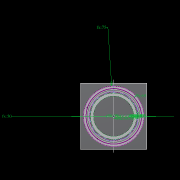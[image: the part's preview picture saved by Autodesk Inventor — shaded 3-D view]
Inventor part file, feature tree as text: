
AUTODESK INVENTOR PART (.ipt)
format: ipt  version: 2022.2 (Build 262287010, 287A)  size: 587,776 bytes
history: native  units: mm
features: other x19, extrude x19, sketch x12, pattern_circular x9, plane x3, fillet x2, move_body x2, revolve x2, draft x2, chamfer x2
ambient origin geometry x8: Origin, YZ Plane, XZ Plane, XY Plane, X Axis, Y Axis, Z Axis, Center Point
bodies: Solid5 (feature_tree)
feature tree (72):
  other  "CrossSection1"
  sketch  "Sketch7"  dims[d90=61.984365mm]
  other  "Roller1"
  other  "Roller2"
  sketch  "Sketch22"  dims[d167=8.972256mm]
  sketch  "Sketch2"  dims[d57=4.025mm]
  sketch  "Sketch23"  dims[d173=10.814812mm]
  other  "RevRoller1"
  fillet  "Fillet1"  Radius=59.246882mm
  pattern_circular  "Circular Pattern13"  Count=360  [1 undecoded]
  move_body  "Move Body7"
  revolve  "Revolution13"  [1 undecoded]
  fillet  "Fillet3"  Radius=0.025mm
  pattern_circular  "Circular Pattern14"  [2 undecoded]
  move_body  "Move Body6"
  revolve  "Revolution14"  [1 undecoded]
  other  "OuterRim_Top2"
  other  "OuterRim_Bottom2"
  plane  "Work Plane7"
  sketch  "Sketch47"  dims[d349=47.575591mm]
  sketch  "Sketch48"  dims[d350=47.575427mm]
  extrude  "Extrusion39"  Depth=50.0mm
  extrude  "Extrusion40"  Depth=50.0mm
  pattern_circular  "Circular Pattern28"  Angle=360.0deg  [1 undecoded]
  sketch  "Sketch49"  dims[d351=0.025mm d352=0.025mm d354=0.1mm d355=16.1595mm d356=16.159664mm d358=360.0deg d359=0.5mm d360=240.0mm d361=360.0deg d363=1.308997mm d367=8.1mm d370=0.1mm d371=1.0mm d372=1.308997mm d373=90.0deg d374=0.5mm d375=240.0mm d376=360.0deg d378=90.0deg d379=0.1mm d380=0.1mm d381=0.1mm d382=0.1mm d383=0.1mm d384=11.193516mm d385=0.0mm d386=0.0mm d391=50.0mm d392=75.0mm d393=1.5mm d394=1.5mm d395=1.5mm d396=1.5mm d397=90.0deg d398=90.0deg d399=90.0deg d400=75.0mm d401=11.193516mm d402=0.0mm d486=0.436332mm d487=0.5mm d488=2.0mm d489=0.0mm d490=20.0mm d495=2.5mm d496=8.0mm d506=13.856406mm d507=55.5mm d508=8.0mm d509=0.05mm d510=2.5mm d511=30.0deg d512=12.0mm d513=6.0mm d514=0.2mm d515=30.0deg d516=131.0mm d517=65.5mm d518=0.2mm d519=100.0mm d520=120.0mm d521=2.0mm d522=150.0mm d530=50.0mm d531=5.5mm d532=5.5mm d533=5.5mm d534=85.75mm d535=73.5mm d536=61.25mm d537=24.5mm d538=3.0mm d539=2.4mm d540=0.0mm d541=0.0mm d542=0.0mm d543=5.5mm d544=3.0mm d545=0.0mm d546=90.0mm d547=360.0deg d549=3.0mm d550=3.0mm d551=2.4mm d552=0.0mm d553=5.596758mm d554=0.0mm d555=2.4mm d556=0.0mm d557=5.596758mm d558=0.0mm d559=5.596758mm d560=0.0mm d561=90.0mm d562=360.0deg d564=60.0mm d565=360.0deg d567=5.5mm d568=5.5mm d569=3.0mm d570=0.0mm d571=5.596758mm d572=0.0mm d573=3.0mm d574=0.0mm d575=5.596758mm d576=0.0mm d577=90.0mm d578=360.0deg d580=60.0mm d581=360.0deg d584=20.0mm d585=8.0mm d587=1.75mm d589=3.0mm d592=2.0mm d593=12.0mm d594=12.0mm d600=0.5mm d601=2.0mm d602=45.0deg d603=0.5mm d604=2.0mm d605=45.0deg d606=0.436332mm d607=0.5mm d608=0.0mm d609=20.0mm d611=360.0deg d613=0.0mm d614=0.0mm d617=0.99971mm d618=100.0mm d620=69.0mm d621=3.0mm d622=5.5mm d623=5.596758mm d624=0.0mm d625=3.0mm d626=0.0mm d627=60.0mm d628=360.0deg d630=5.5mm d631=3.0mm d632=5.596758mm d633=0.0mm d634=2.593516mm d635=0.0mm d636=50.0mm d637=360.0deg d16=0.872665mm d17=0.872665mm d49=0.872665mm d50=0.872665mm d51=0.872665mm d52=0.872665mm d236=0.5mm d237=0.872665mm d238=0.5mm d239=0.872665mm d282=1.0mm d283=1.0mm d284=1.0mm d285=0.15mm d286=0.25mm d287=0.375mm d288=14.3117mm d289=0.75mm d290=20.594885mm d291=0.0625mm d292=0.75mm d293=0.375mm d405=0.5mm d406=0.872665mm d407=0.5mm d408=0.872665mm d413=0.5mm d414=0.872665mm d415=0.5mm d416=0.872665mm d417=0.5mm d418=0.872665mm d419=0.5mm d420=0.872665mm d421=0.872665mm d431=0.5mm d432=0.872665mm d433=0.5mm d434=0.872665mm d471=0.5mm d472=0.872665mm d473=0.5mm d474=0.872665mm d497=0.5mm d498=0.872665mm d499=0.5mm d500=0.872665mm d590=0.5mm d591=0.872665mm]
  extrude  "Extrusion41"  Depth=50.0mm
  extrude  "Extrusion42"  Depth=50.0mm
  pattern_circular  "Circular Pattern29"  Angle=360.0deg  [1 undecoded]
  extrude  "Rotor_Ring"  Depth=50.0mm
  draft  "FaceDraft2"
  sketch  "Sketch30"  dims[d201=75.0mm d232=0.0mm d233=3600.0mm]
  plane  "Work Plane5"
  other  "Rotor Featurs"
  other  "RotorRim_Bottom"
  extrude  "Extrusion24"  Depth=50.0mm
  extrude  "Extrusion25"  Depth=0.1mm
  extrude  "Extrusion26"  Depth=50.0mm
  pattern_circular  "Circular Pattern23"  [2 undecoded]
  sketch  "Sketch41"  dims[d346=0.025mm]
  extrude  "Extrusion27"  TaperAngle=90.0deg  [1 undecoded]
  extrude  "Extrusion28"  Depth=50.0mm
  pattern_circular  "Circular Pattern24"  Count=24  [1 undecoded]
  extrude  "Extrusion29"  TaperAngle=360.0deg  [1 undecoded]
  extrude  "Extrusion30"  TaperAngle=90.0deg  [1 undecoded]
  extrude  "Extrusion31"  Depth=0.1mm
  pattern_circular  "Circular Pattern25"  [2 undecoded]
  sketch  "Sketch42"  dims[d347=0.1mm]
  extrude  "Extrusion32"  Depth=0.1mm
  extrude  "Extrusion33"  Depth=0.1mm
  extrude  "Extrusion34"  Depth=0.1mm
  extrude  "Extrusion35"  Depth=11.193516mm
  pattern_circular  "Circular Pattern26"  [2 undecoded]
  pattern_circular  "Circular Pattern27"  [2 undecoded]
  chamfer  "Chamfer1"  Distance=50.0mm
  chamfer  "Chamfer2"  Distance=75.0mm
  draft  "FaceDraft4"
  plane  "Work Plane6"
  sketch  "Sketch43"  dims[d348=0.1mm]
  extrude  "Extrusion37"  Depth=1.5mm
  extrude  "Extrusion38"  Depth=1.5mm
  other  "2D Equation Curve1"
  sketch  "Sketch40"  dims[d343=16.1595mm d344=16.159664mm d345=0.025mm]
  other  "Work Axis6"
  other  "Work Axis7"
  other  "Work Axis8"
  other  "Work Axis9"
  other  "Work Axis10"
  other  "Work Point1"
  other  "Work Point2"
  other  "Work Point3"
  other  "Work Point4"
  other  "Work Point5"
note: 19 required parameter values undecoded (feature->parameter linkage not recoverable at this tier; creation-order binding heuristic only, values carry confidence <= 0.55)